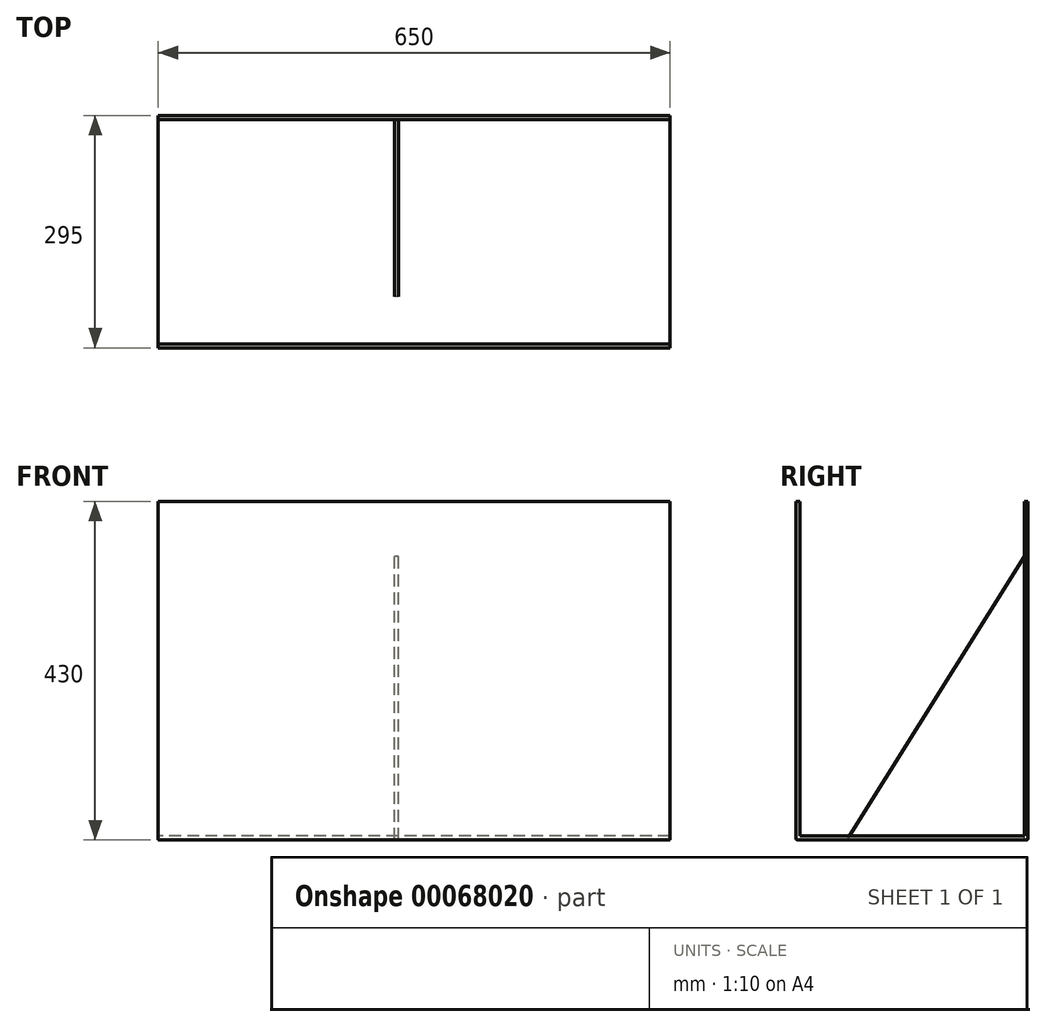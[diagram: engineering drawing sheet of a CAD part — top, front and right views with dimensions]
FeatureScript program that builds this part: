
annotation { "Feature Type Name" : "Feature", "Feature Type Description" : "" }
export const myFeature = defineFeature(function(context is Context, id is Id, definition is map)
    precondition{}
    {
        {
            var Q0;
            Q0=qCreatedBy(makeId("Right.planeOp"),FACE);
            var sketch = newSketch(context, id + "F0", { "sketchPlane" : qUnion([Q0])});
            skLineSegment(sketch, "E0.left", {"start": v(0, 0) * mm, "end": v(0, 430) * mm});
            skLineSegment(sketch, "E1", {"start": v(0, 0) * mm, "end": v(-295, 0) * mm});
            skLineSegment(sketch, "E2", {"start": v(-295, 0) * mm, "end": v(-295, 430) * mm});
            skLineSegment(sketch, "E3.0", {"start": v(-290, 5) * mm, "end": v(-290, 430) * mm});
            skLineSegment(sketch, "E3.1", {"start": v(-5, 5) * mm, "end": v(-290, 5) * mm});
            skLineSegment(sketch, "E3.2", {"start": v(-5, 5) * mm, "end": v(-5, 430) * mm});
            skLineSegment(sketch, "E4", {"start": v(0, 430) * mm, "end": v(-5, 430) * mm});
            skLineSegment(sketch, "E5", {"start": v(-290, 430) * mm, "end": v(-295, 430) * mm});
            skSolve(sketch);
        }
        {
            var Q0;
            Q0=makeQuery(id+"F0.imprint","IMPRINT",FACE,{"disambiguationData":[TD([[makeQuery(id+"F0.imprint","IMPRINT",EDGE,{"derivedFrom":sQuery(id+"F0.wireOp",EDGE,"E0.bottom")}),-1.0]])]});
            var Q1;
            Q1=makeQuery(id+"F0.imprint","IMPRINT",FACE,{"disambiguationData":[TD([[makeQuery(id+"F0.imprint","IMPRINT",EDGE,{"derivedFrom":sQuery(id+"F0.wireOp",EDGE,"E0.left")}),1.0]])]});
            extrude(context, id + "F1", {"entities" : qUnion([Q0, Q1]), "depth" : 650 * mm});
        }
        {
            var Q0;
            Q0=qCreatedBy(makeId("Right.planeOp"),FACE);
            cPlane(context, id + "F2", {"entities" : qUnion([Q0]), "cplaneType" : CPlaneType.OFFSET, "offset" : 300 * mm, "width" : 150 * mm, "height" : 150 * mm});
        }
        {
            var Q0;
            Q0=qCreatedBy(id+"F2.planeOp",FACE);
            var sketch = newSketch(context, id + "F3", { "sketchPlane" : qUnion([Q0])});
            skLineSegment(sketch, "E6.0", {"start": v(-5, 0) * mm, "end": v(-5, 360) * mm});
            skLineSegment(sketch, "E7.0", {"start": v(-5, 0) * mm, "end": v(-230, 0) * mm});
            skPoint(sketch, "E8", {"position": v(-230, 0) * mm});
            skPoint(sketch, "E9", {"position": v(-5, 360) * mm});
            skLineSegment(sketch, "E10", {"start": v(-5, 360) * mm, "end": v(-230, 0) * mm});
            skSolve(sketch);
        }
        {
            var Q0;
            Q0=makeQuery(id+"F3.imprint","IMPRINT",FACE,{"disambiguationData":[TD([[makeQuery(id+"F3.imprint","IMPRINT",EDGE,{"derivedFrom":sQuery(id+"F3.wireOp",EDGE,"E6.0")}),1.0]])]});
            extrude(context, id + "F4", {"entities" : qUnion([Q0]), "depth" : 5 * mm});
        }
        {
            var Q0;
            Q0=makeQuery(id+"F1.opExtrude","SWEPT_EDGE",EDGE,{"disambiguationData":[OSD([sQuery(id+"F0.wireOp",EDGE,"E0.left"),sQuery(id+"F0.wireOp",EDGE,"E1")])]});
            var Q1;
            Q1=makeQuery(id+"F1.opExtrude","SWEPT_EDGE",EDGE,{"disambiguationData":[OSD([sQuery(id+"F0.wireOp",EDGE,"E1"),sQuery(id+"F0.wireOp",EDGE,"E2")])]});
            fillet(context, id + "F5", {"entities" : qUnion([Q0, Q1]), "radius" : 2 * mm, "tangentPropagation" : true, "allowEdgeOverflow" : false});
        }
    });
